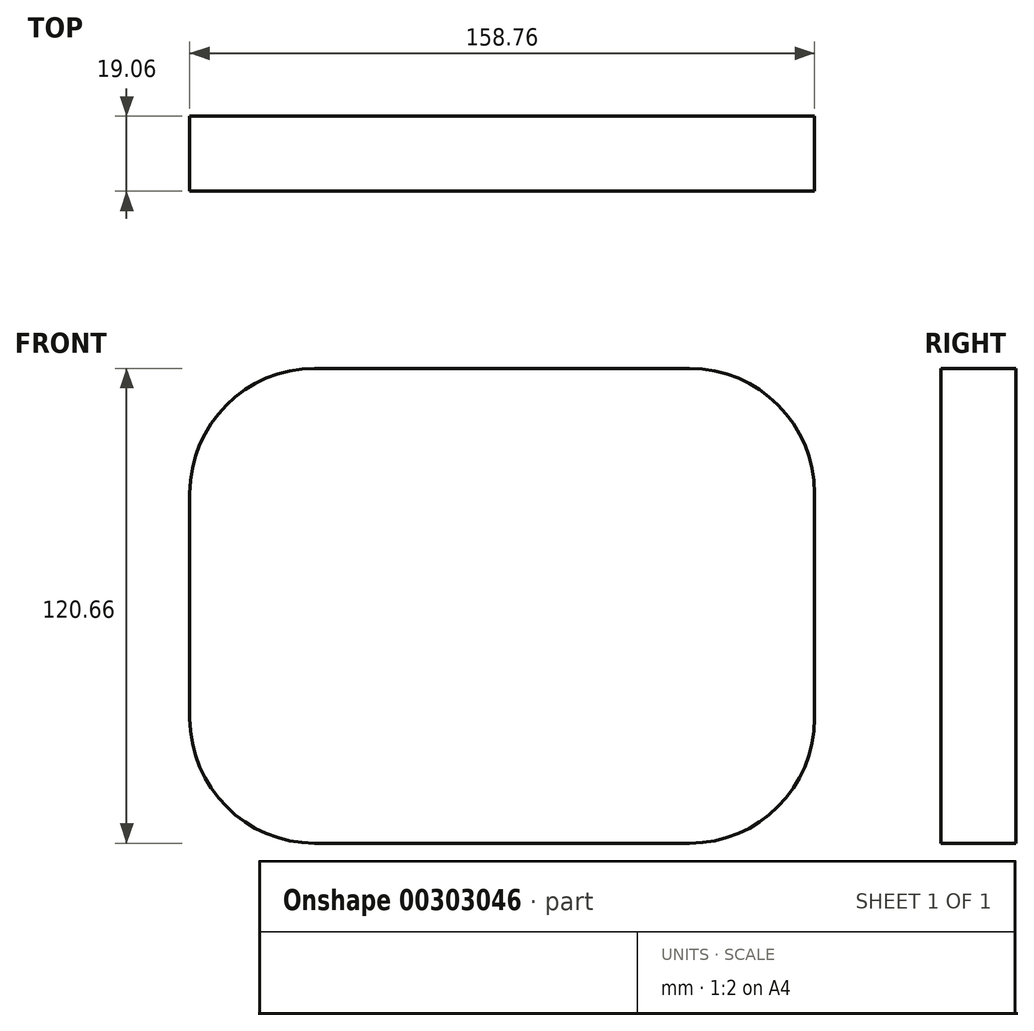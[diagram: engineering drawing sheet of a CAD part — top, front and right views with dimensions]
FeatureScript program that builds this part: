
annotation { "Feature Type Name" : "Feature", "Feature Type Description" : "" }
export const myFeature = defineFeature(function(context is Context, id is Id, definition is map)
    precondition{}
    {
        {
            var Q0;
            Q0=qCreatedBy(makeId("Front.planeOp"),FACE);
            var sketch = newSketch(context, id + "F0", { "sketchPlane" : qUnion([Q0])});
            skLineSegment(sketch, "E0", {"start": v(-79.38, -28.58) * mm, "end": v(-79.38, 28.58) * mm});
            skLineSegment(sketch, "E1", {"start": v(-47.62, 60.33) * mm, "end": v(47.62, 60.33) * mm});
            skLineSegment(sketch, "E2", {"start": v(79.38, 28.58) * mm, "end": v(79.38, -28.58) * mm});
            skLineSegment(sketch, "E3", {"start": v(47.62, -60.32) * mm, "end": v(-47.62, -60.33) * mm});
            skArc(sketch, "E4", {"start": v(-79.38, 28.58) * mm, "mid": v(-70.08, 51.03) * mm, "end": v(-47.62, 60.33) * mm});
            skArc(sketch, "E5.MirrorCS", {"start": v(79.38, 28.58) * mm, "mid": v(70.08, 51.03) * mm, "end": v(47.62, 60.33) * mm});
            skArc(sketch, "E6.MirrorCS", {"start": v(79.38, -28.58) * mm, "mid": v(70.08, -51.03) * mm, "end": v(47.62, -60.33) * mm});
            skArc(sketch, "E7.MirrorCS", {"start": v(-79.38, -28.58) * mm, "mid": v(-70.08, -51.03) * mm, "end": v(-47.62, -60.33) * mm});
            skSolve(sketch);
        }
        {
            var Q0;
            Q0=makeQuery(id+"F0.imprint","IMPRINT",FACE,{"disambiguationData":[TD([[makeQuery(id+"F0.imprint","IMPRINT",EDGE,{"derivedFrom":sQuery(id+"F0.wireOp",EDGE,"E0")}),-1.0]])]});
            extrude(context, id + "F1", {"entities" : qUnion([Q0]), "depth" : 19.05 * mm, "symmetric" : true});
        }
    });
